# Revit family: AFX-Ally-LED_Ceiling-1
name_source: partatom
category: Lighting Fixtures
units: mm (PartAtom-declared; Revit-internal decimal feet)

## family parameters
Cut with Voids When Loaded = No
Host = Face
Light Source = Yes
Part Type = Normal
Room Calculation Point = No
Round Connector Dimension = Use Diameter
Shared = No

## types (5) — shared parameters
Apparent Load = 0 VA
Assembly Code = D5020200
Body Finish = AFX - White Steel
Color Filter = 16777215
Colour Rendering Index = 90
Default Elevation = 48"
Depth = 4"
Diameter = 16"
Diffuser Finish = AFX - White Acrylic
Dimming Lamp Color Temperature Shift = <None>
Emit Shape Visible in Rendering = No
Emit from Circle Diameter = 12"
Keynote = 12500
Manufacturer = AFX Inc
Product Documentation Link = https://www.afxinc.com
Revit File Built By = https://servex-us.com
Screen Finish = AFX - White Steel
Sustainability = https://lamprecycle.org
Tilt Angle = 90.00°
Type Comments = Ally
URL = https://www.afxinc.com
Voltage = 120 V
Wattage Comments = 15W

## per-type parameters (varying)
| type | Description | Photometric Web File |
| ALYF16LAJD1WH-2700K | LED Ceiling - CCT 2700K - 16"Dia x 4"D | ALYF16LAJDIWH_ 2700K IES.IES |
| ALYF16LAJD1WH-3500K | LED Ceiling - CCT 3500K - 16"Dia x 4"D | ALYF16LAJDIWH_ 3500K IES.IES |
| ALYF16LAJD1WH-3000K | LED Ceiling - CCT 3000K - 16"Dia x 4"D | ALYF16LAJDIWH_ 3000K IES.IES |
| ALYF16LAJD1WH-4000K | LED Ceiling - CCT 4000K - 16"Dia x 4"D | ALYF16LAJDIWH_ 4000K IES.IES |
| ALYF16LAJD1WH-5000K | LED Ceiling - CCT 4000K - 16"Dia x 4"D | ALYF16LAJDIWH_ 5000K IES.IES |

note: column(s) folded — value = type name in every type: Model

## geometry (parser evidence)
native form markers: Sweep x3
no freeform markers — native parametric forms only
